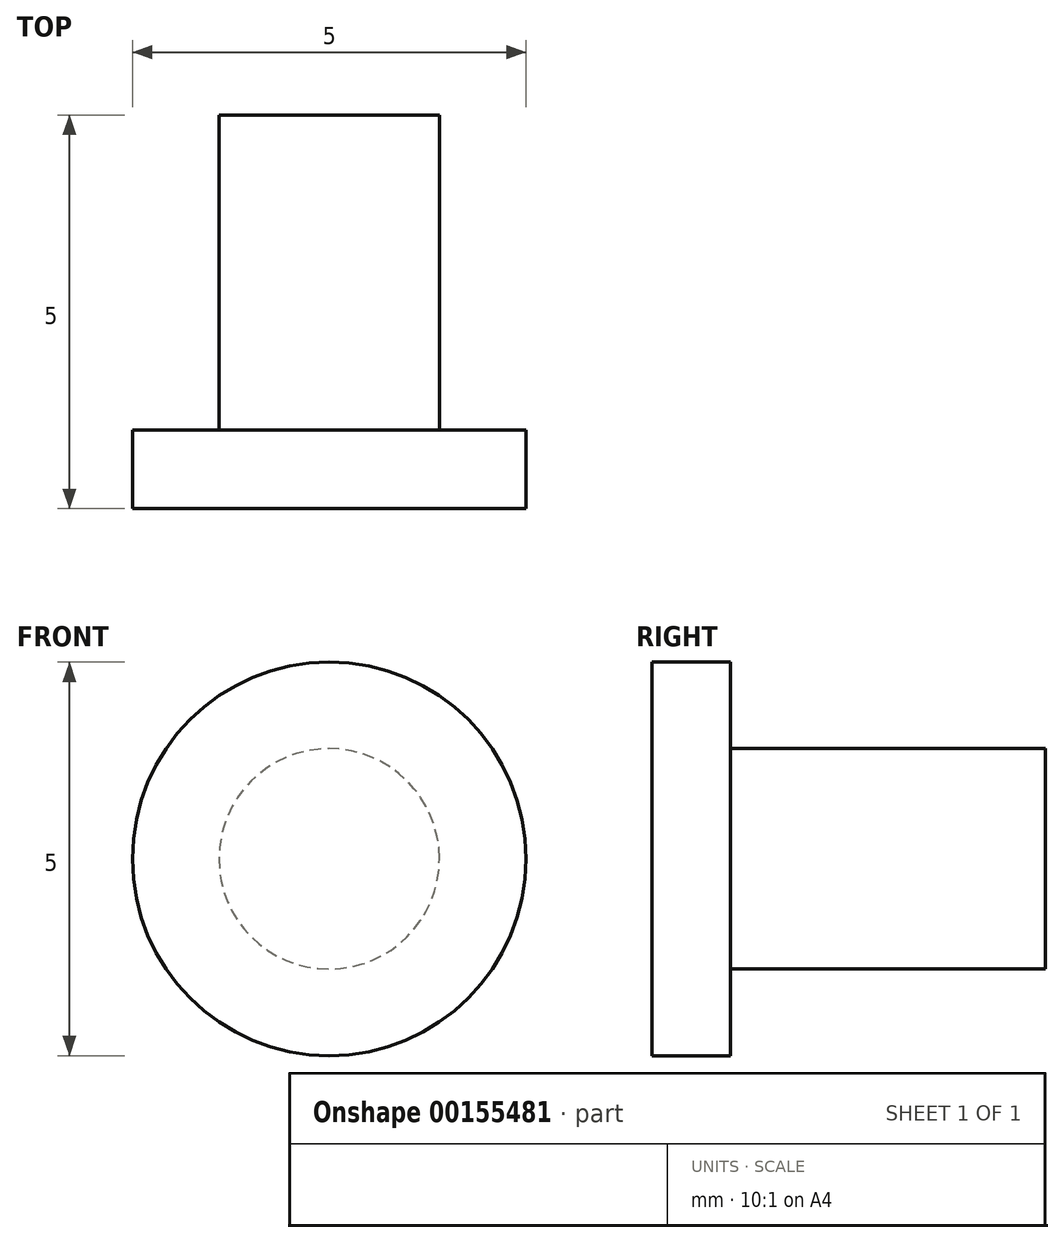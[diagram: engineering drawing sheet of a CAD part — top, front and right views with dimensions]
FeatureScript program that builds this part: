
annotation { "Feature Type Name" : "Feature", "Feature Type Description" : "" }
export const myFeature = defineFeature(function(context is Context, id is Id, definition is map)
    precondition{}
    {
        {
            var Q0;
            Q0=qCreatedBy(makeId("Front.planeOp"),FACE);
            var sketch = newSketch(context, id + "F0", { "sketchPlane" : qUnion([Q0])});
            skCircle(sketch, "E0", {"center": v(0, 0) * mm, "radius": 2.5 * mm});
            skCircle(sketch, "E1", {"center": v(0, 0) * mm, "radius": 1.4 * mm});
            skSolve(sketch);
        }
        {
            var Q0;
            Q0=makeQuery(id+"F0.imprint","IMPRINT",FACE,{"disambiguationData":[TD([[makeQuery(id+"F0.imprint","IMPRINT",EDGE,{"derivedFrom":sQuery(id+"F0.wireOp",EDGE,"E0")}),1.0]])]});
            var Q1;
            Q1=makeQuery(id+"F0.imprint","IMPRINT",FACE,{"disambiguationData":[TD([[makeQuery(id+"F0.imprint","IMPRINT",EDGE,{"derivedFrom":sQuery(id+"F0.wireOp",EDGE,"E1")}),1.0]])]});
            extrude(context, id + "F1", {"entities" : qUnion([Q0, Q1]), "oppositeDirection" : true, "depth" : 1 * mm});
        }
        {
            var Q0;
            Q0=makeQuery(id+"F0.imprint","IMPRINT",FACE,{"disambiguationData":[TD([[makeQuery(id+"F0.imprint","IMPRINT",EDGE,{"derivedFrom":sQuery(id+"F0.wireOp",EDGE,"E1")}),1.0]])]});
            extrude(context, id + "F2", {"entities" : qUnion([Q0]), "operationType" : NewBodyOperationType.ADD, "oppositeDirection" : true, "depth" : 5 * mm});
        }
    });
